# Revit family: 54-3334-001 DN1200
name_source: partatom
category: Pipe Accessories
units: mm (PartAtom-declared; Revit-internal decimal feet)

## family parameters
Always vertical = No
Cut with Voids When Loaded = No
Part Type = Valve - Breaks Into
Round Connector Dimension = Use Diameter
Shared = No
Work Plane-Based = No

## types (8) — shared parameters
1 = 1 mm  [stored 0.00328084 ft]
10 = 10 mm  [stored 0.0328084 ft]
20 = 25 mm  [stored 0.082021 ft]
5 = 5 mm  [stored 0.0164042 ft]
50 = 80 mm  [stored 0.262467 ft]
54-1200-33-0302100 = DN1200_ PN10_ CTC
54-1200-33-0303100 = DN1200_ PN10_ CTC
54-1200-33-0304100 = DN1200_ PN10_ CTC
54-1200-33-1302100 = DN1200_ PN16_ CTC
54-1200-33-1303100 = DN1200_ PN16_ CTC
54-1200-33-1304100 = DN1200_ PN16_ CTC
54-1200-34-0302100 = DN1200_ PN10_ CTO
54-1200-34-1302100 = DN1200_ PN16_ CTO
ADN = 1200 mm
BP_centre = 14.5 mm  [stored 0.0475722 ft]
Body_H = 1213.5 mm
Bonnet_dim3 = 2087.22 mm
Bypass_D7 = 697.2 mm
Bypass_DN = 150 mm
Bypass_FL_OD = 210 mm
Bypass_L = 106 mm
Bypass_Location = 259 mm
Bypass_R = 29 mm  [stored 0.0951444 ft]
Bypass_R1 = 58 mm  [stored 0.190289 ft]
Bypass_Vale_D1 = 168 mm
Bypass_Vale_D2 = 147 mm
Bypass_Vale_D3 = 168 mm
Bypass_Vale_D6 = 252 mm
Bypass_W = 90 mm
Bypass_sweep = 697.2 mm
Description_ = AVK GATE VALVE, FLANGED, METAL SEATED, PN10/16
H = 782 mm
H1 = 2427 mm
H2 = 773 mm
L = 914 mm
OD1 = 1546 mm
Raised_dia = 1328 mm
Raised_dis = 5 mm  [stored 0.0164042 ft]
Rib_Actual = 1018 mm
Rib_H = 970.8 mm
Rib_H1 = 410 mm
Rib_H2 = 780 mm
Rib_H3 = 930 mm
Rib_H4 = 1080 mm
Search_table = 54-3334-001 DN1200
Stem_H1 = 225 mm
Stem_H2 = 191.25 mm
Stem_H3 = 303.75 mm
URL product pages = https://www.avkvalves.com
W = 2036 mm
W-W1 = 856 mm
W1 = 1180 mm
W_half = 856 mm
sweep = 6 mm  [stored 0.019685 ft]
sweep_start = 664 mm
zero-valued in all types: Default Elevation

## per-type parameters (varying)
- 54-1200-33-0302100: ACtuator_T=32.4 mm  [stored 0.106299 ft]; Actuator_FLR=105 mm; Actuator_dim1=63 mm  [stored 0.206693 ft]; Actuator_dim2=37.8 mm  [stored 0.124016 ft]; Actuator_dim3=69.3 mm  [stored 0.227362 ft]; Body_L=1354.5 mm; Body_T=542.5 mm; Body_W=538.4 mm; Body_rib_T=18 mm  [stored 0.0590551 ft]; Bonnet_FL_L=1505 mm; Bonnet_FL_T=85.5 mm; Bonnet_FL_W=673 mm; Bonnet_dim1=270.9 mm; Bonnet_dim2=188.44 mm; Bonnet_fillet=59.82 mm; Bore=600 mm; Bypass_Vale_D4=121.14 mm; Bypass_Vale_D5=169.6 mm; Bypass_Vale_T=96.91 mm; Cut_dis=42.75 mm  [stored 0.140256 ft]; DN=1200 mm; F=42 mm  [stored 0.137795 ft]; F1=18.9 mm  [stored 0.0620079 ft]; F2=136 mm; FL_T=45 mm  [stored 0.147638 ft]; Fillet=179.47 mm; OD=1455 mm; PN=10 mm  [stored 0.0328084 ft]; Rib_L=677.25 mm; Rib_W=302.85 mm; Stem_D1=21 mm  [stored 0.0688976 ft]; Stem_D2=31.5 mm  [stored 0.103346 ft]; Stem_dim=52.5 mm  [stored 0.172244 ft]; bottom_rib=727.5 mm; stem_dim=45.33 mm; stem_dim1=68.25 mm  [stored 0.223917 ft]; wedge_dim1=592.24 mm
- 54-1200-33-0303100: ACtuator_T=32.4 mm  [stored 0.106299 ft]; Actuator_FLR=150 mm; Actuator_dim1=90 mm; Actuator_dim2=54 mm  [stored 0.177165 ft]; Actuator_dim3=99 mm; Body_L=1354.5 mm; Body_T=542.5 mm; Body_W=538.4 mm; Body_rib_T=18 mm  [stored 0.0590551 ft]; Bonnet_FL_L=1505 mm; Bonnet_FL_T=85.5 mm; Bonnet_FL_W=673 mm; Bonnet_dim1=270.9 mm; Bonnet_dim2=188.44 mm; Bonnet_fillet=59.82 mm; Bore=600.05 mm; Bypass_Vale_D4=121.14 mm; Bypass_Vale_D5=169.6 mm; Bypass_Vale_T=96.91 mm; Cut_dis=42.75 mm  [stored 0.140256 ft]; DN=1200.1 mm; F=60 mm  [stored 0.19685 ft]; F1=27 mm  [stored 0.0885827 ft]; F2=176 mm; FL_T=45 mm  [stored 0.147638 ft]; Fillet=179.47 mm; OD=1455 mm; PN=10 mm  [stored 0.0328084 ft]; Rib_L=677.25 mm; Rib_W=302.85 mm; Stem_D1=30 mm  [stored 0.0984252 ft]; Stem_D2=45 mm  [stored 0.147638 ft]; Stem_dim=75 mm; bottom_rib=727.5 mm; stem_dim=58.67 mm; stem_dim1=97.5 mm; wedge_dim1=592.24 mm
- 54-1200-33-0304100: ACtuator_T=32.4 mm  [stored 0.106299 ft]; Actuator_FLR=175 mm; Actuator_dim1=105 mm; Actuator_dim2=63 mm  [stored 0.206693 ft]; Actuator_dim3=115.5 mm; Body_L=1354.5 mm; Body_T=542.5 mm; Body_W=538.4 mm; Body_rib_T=18 mm  [stored 0.0590551 ft]; Bonnet_FL_L=1505 mm; Bonnet_FL_T=85.5 mm; Bonnet_FL_W=673 mm; Bonnet_dim1=270.9 mm; Bonnet_dim2=188.44 mm; Bonnet_fillet=59.82 mm; Bore=600.06 mm; Bypass_Vale_D4=121.14 mm; Bypass_Vale_D5=169.6 mm; Bypass_Vale_T=96.91 mm; Cut_dis=42.75 mm  [stored 0.140256 ft]; DN=1200.11 mm; F=70 mm  [stored 0.229659 ft]; F1=31.5 mm  [stored 0.103346 ft]; F2=206 mm; FL_T=45 mm  [stored 0.147638 ft]; Fillet=179.47 mm; OD=1455 mm; PN=10 mm  [stored 0.0328084 ft]; Rib_L=677.25 mm; Rib_W=302.85 mm; Stem_D1=35 mm  [stored 0.114829 ft]; Stem_D2=52.5 mm  [stored 0.172244 ft]; Stem_dim=87.5 mm; bottom_rib=727.5 mm; stem_dim=68.67 mm; stem_dim1=113.75 mm; wedge_dim1=592.24 mm
- 54-1200-33-1302100: ACtuator_T=41.04 mm  [stored 0.134646 ft]; Actuator_FLR=105 mm; Actuator_dim1=63 mm  [stored 0.206693 ft]; Actuator_dim2=37.8 mm  [stored 0.124016 ft]; Actuator_dim3=69.3 mm  [stored 0.227362 ft]; Body_L=1354.5 mm; Body_T=542.5 mm; Body_W=538.4 mm; Body_rib_T=22.8 mm  [stored 0.0748031 ft]; Bonnet_FL_L=1505 mm; Bonnet_FL_T=108.3 mm; Bonnet_FL_W=673 mm; Bonnet_dim1=270.9 mm; Bonnet_dim2=188.44 mm; Bonnet_fillet=59.82 mm; Bore=600.06 mm; Bypass_Vale_D4=121.14 mm; Bypass_Vale_D5=169.6 mm; Bypass_Vale_T=96.91 mm; Cut_dis=54.15 mm  [stored 0.177657 ft]; DN=1200.12 mm; F=42 mm  [stored 0.137795 ft]; F1=18.9 mm  [stored 0.0620079 ft]; F2=136 mm; FL_T=57 mm  [stored 0.187008 ft]; Fillet=179.47 mm; OD=1400 mm; PN=16 mm  [stored 0.0524934 ft]; Rib_L=677.25 mm; Rib_W=302.85 mm; Stem_D1=21 mm  [stored 0.0688976 ft]; Stem_D2=31.5 mm  [stored 0.103346 ft]; Stem_dim=52.5 mm  [stored 0.172244 ft]; bottom_rib=700 mm; stem_dim=45.33 mm; stem_dim1=68.25 mm  [stored 0.223917 ft]; wedge_dim1=592.24 mm
- 54-1200-33-1303100: ACtuator_T=41.04 mm  [stored 0.134646 ft]; Actuator_FLR=150 mm; Actuator_dim1=90 mm; Actuator_dim2=54 mm  [stored 0.177165 ft]; Actuator_dim3=99 mm; Body_L=1521 mm; Body_T=592.5 mm; Body_W=446.4 mm; Body_rib_T=22.8 mm  [stored 0.0748031 ft]; Bonnet_FL_L=1690 mm; Bonnet_FL_T=108.3 mm; Bonnet_FL_W=558 mm; Bonnet_dim1=304.2 mm; Bonnet_dim2=156.24 mm; Bonnet_fillet=49.6 mm  [stored 0.16273 ft]; Bore=600.07 mm; Bypass_Vale_D4=100.44 mm; Bypass_Vale_D5=140.62 mm; Bypass_Vale_T=80.35 mm; Cut_dis=54.15 mm  [stored 0.177657 ft]; DN=1200.13 mm; F=60 mm  [stored 0.19685 ft]; F1=27 mm  [stored 0.0885827 ft]; F2=176 mm; FL_T=57 mm  [stored 0.187008 ft]; Fillet=148.8 mm; OD=1546 mm; PN=16 mm  [stored 0.0524934 ft]; Rib_L=760.5 mm; Rib_W=251.1 mm; Stem_D1=30 mm  [stored 0.0984252 ft]; Stem_D2=45 mm  [stored 0.147638 ft]; Stem_dim=75 mm; bottom_rib=773 mm; stem_dim=58.67 mm; stem_dim1=97.5 mm; wedge_dim1=491.04 mm
- 54-1200-33-1304100: ACtuator_T=41.04 mm  [stored 0.134646 ft]; Actuator_FLR=175 mm; Actuator_dim1=105 mm; Actuator_dim2=63 mm  [stored 0.206693 ft]; Actuator_dim3=115.5 mm; Body_L=1521 mm; Body_T=592.5 mm; Body_W=446.4 mm; Body_rib_T=22.8 mm  [stored 0.0748031 ft]; Bonnet_FL_L=1690 mm; Bonnet_FL_T=108.3 mm; Bonnet_FL_W=558 mm; Bonnet_dim1=304.2 mm; Bonnet_dim2=156.24 mm; Bonnet_fillet=49.6 mm  [stored 0.16273 ft]; Bore=600.07 mm; Bypass_Vale_D4=100.44 mm; Bypass_Vale_D5=140.62 mm; Bypass_Vale_T=80.35 mm; Cut_dis=54.15 mm  [stored 0.177657 ft]; DN=1200.14 mm; F=70 mm  [stored 0.229659 ft]; F1=31.5 mm  [stored 0.103346 ft]; F2=206 mm; FL_T=57 mm  [stored 0.187008 ft]; Fillet=148.8 mm; OD=1546 mm; PN=16 mm  [stored 0.0524934 ft]; Rib_L=760.5 mm; Rib_W=251.1 mm; Stem_D1=35 mm  [stored 0.114829 ft]; Stem_D2=52.5 mm  [stored 0.172244 ft]; Stem_dim=87.5 mm; bottom_rib=773 mm; stem_dim=68.67 mm; stem_dim1=113.75 mm; wedge_dim1=491.04 mm
- 54-1200-34-0302100: ACtuator_T=32.4 mm  [stored 0.106299 ft]; Actuator_FLR=105 mm; Actuator_dim1=63 mm  [stored 0.206693 ft]; Actuator_dim2=37.8 mm  [stored 0.124016 ft]; Actuator_dim3=69.3 mm  [stored 0.227362 ft]; Body_L=1521 mm; Body_T=592.5 mm; Body_W=446.4 mm; Body_rib_T=18 mm  [stored 0.0590551 ft]; Bonnet_FL_L=1690 mm; Bonnet_FL_T=85.5 mm; Bonnet_FL_W=558 mm; Bonnet_dim1=304.2 mm; Bonnet_dim2=156.24 mm; Bonnet_fillet=49.6 mm  [stored 0.16273 ft]; Bore=600.08 mm; Bypass_Vale_D4=100.44 mm; Bypass_Vale_D5=140.62 mm; Bypass_Vale_T=80.35 mm; Cut_dis=42.75 mm  [stored 0.140256 ft]; DN=1200.15 mm; F=42 mm  [stored 0.137795 ft]; F1=18.9 mm  [stored 0.0620079 ft]; F2=136 mm; FL_T=45 mm  [stored 0.147638 ft]; Fillet=148.8 mm; OD=1455 mm; PN=10 mm  [stored 0.0328084 ft]; Rib_L=760.5 mm; Rib_W=251.1 mm; Stem_D1=21 mm  [stored 0.0688976 ft]; Stem_D2=31.5 mm  [stored 0.103346 ft]; Stem_dim=52.5 mm  [stored 0.172244 ft]; bottom_rib=727.5 mm; stem_dim=45.33 mm; stem_dim1=68.25 mm  [stored 0.223917 ft]; wedge_dim1=491.04 mm
- 54-1200-34-1302100: ACtuator_T=41.04 mm  [stored 0.134646 ft]; Actuator_FLR=105 mm; Actuator_dim1=63 mm  [stored 0.206693 ft]; Actuator_dim2=37.8 mm  [stored 0.124016 ft]; Actuator_dim3=69.3 mm  [stored 0.227362 ft]; Body_L=1521 mm; Body_T=592.5 mm; Body_W=446.4 mm; Body_rib_T=22.8 mm  [stored 0.0748031 ft]; Bonnet_FL_L=1690 mm; Bonnet_FL_T=108.3 mm; Bonnet_FL_W=558 mm; Bonnet_dim1=304.2 mm; Bonnet_dim2=156.24 mm; Bonnet_fillet=49.6 mm  [stored 0.16273 ft]; Bore=600.08 mm; Bypass_Vale_D4=100.44 mm; Bypass_Vale_D5=140.62 mm; Bypass_Vale_T=80.35 mm; Cut_dis=54.15 mm  [stored 0.177657 ft]; DN=1200.16 mm; F=42 mm  [stored 0.137795 ft]; F1=18.9 mm  [stored 0.0620079 ft]; F2=136 mm; FL_T=57 mm  [stored 0.187008 ft]; Fillet=148.8 mm; OD=1546 mm; PN=16 mm  [stored 0.0524934 ft]; Rib_L=760.5 mm; Rib_W=251.1 mm; Stem_D1=21 mm  [stored 0.0688976 ft]; Stem_D2=31.5 mm  [stored 0.103346 ft]; Stem_dim=52.5 mm  [stored 0.172244 ft]; bottom_rib=773 mm; stem_dim=45.33 mm; stem_dim1=68.25 mm  [stored 0.223917 ft]; wedge_dim1=491.04 mm

note: [stored X ft] marks values corroborated as IEEE doubles in the binary element streams (Revit-internal decimal feet)

## geometry (parser evidence)
native form markers: Sweep x4
no freeform markers — native parametric forms only
